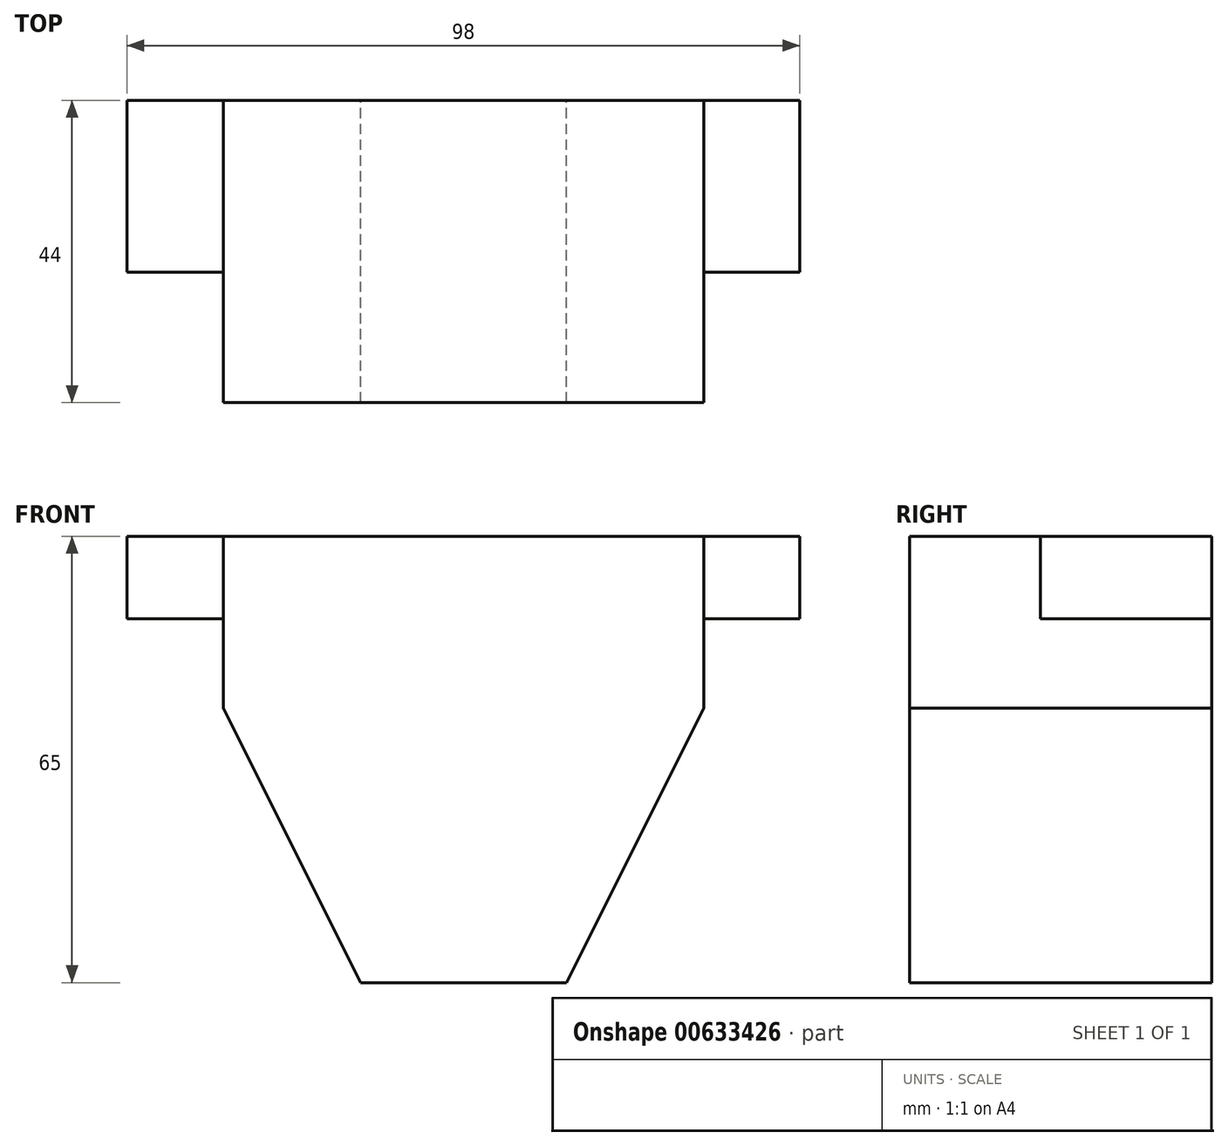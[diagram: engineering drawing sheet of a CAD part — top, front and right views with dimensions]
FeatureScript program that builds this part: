
annotation { "Feature Type Name" : "Feature", "Feature Type Description" : "" }
export const myFeature = defineFeature(function(context is Context, id is Id, definition is map)
    precondition{}
    {
        {
            var Q0;
            Q0=qCreatedBy(makeId("Front.planeOp"),FACE);
            var sketch = newSketch(context, id + "F0", { "sketchPlane" : qUnion([Q0])});
            skLineSegment(sketch, "E0.bottom", {"start": v(-35, -12.5) * mm, "end": v(35, -12.5) * mm});
            skLineSegment(sketch, "E0.top", {"start": v(-35, 12.5) * mm, "end": v(35, 12.5) * mm});
            skLineSegment(sketch, "E0.left", {"start": v(-35, -12.5) * mm, "end": v(-35, 12.5) * mm});
            skLineSegment(sketch, "E0.right", {"start": v(35, -12.5) * mm, "end": v(35, 12.5) * mm});
            skPoint(sketch, "E0.middle", {"position": v(0, 0) * mm});
            skLineSegment(sketch, "E1", {"start": v(-35, 12.5) * mm, "end": v(-49, 12.5) * mm});
            skLineSegment(sketch, "E2", {"start": v(-49, 12.5) * mm, "end": v(-49, 0.5) * mm});
            skLineSegment(sketch, "E3", {"start": v(-49, 0.5) * mm, "end": v(-35, 0.5) * mm});
            skLineSegment(sketch, "E4", {"start": v(35, 12.5) * mm, "end": v(49, 12.5) * mm});
            skLineSegment(sketch, "E5", {"start": v(49, 12.5) * mm, "end": v(49, 0.5) * mm});
            skLineSegment(sketch, "E6", {"start": v(49, 0.5) * mm, "end": v(35, 0.5) * mm});
            skLineSegment(sketch, "E7", {"start": v(-15, -52.5) * mm, "end": v(15, -52.5) * mm});
            skLineSegment(sketch, "E8", {"start": v(-15, -52.5) * mm, "end": v(-35, -12.5) * mm});
            skLineSegment(sketch, "E9", {"start": v(35, -12.5) * mm, "end": v(15, -52.5) * mm});
            skSolve(sketch);
        }
        {
            var Q0;
            {var subQ0=sQuery(id+"F0.wireOp",EDGE,"E1");Q0=makeQuery(id+"F0.imprint","IMPRINT",FACE,{"disambiguationData":[TD([[makeQuery(id+"F0.imprint","IMPRINT",EDGE,{"derivedFrom":subQ0}),1.0]])]});}
            var Q1;
            {var subQ0=sQuery(id+"F0.wireOp",EDGE,"E4");Q1=makeQuery(id+"F0.imprint","IMPRINT",FACE,{"disambiguationData":[TD([[makeQuery(id+"F0.imprint","IMPRINT",EDGE,{"derivedFrom":subQ0}),-1.0]])]});}
            extrude(context, id + "F1", {"entities" : qUnion([Q0, Q1]), "depth" : 25 * mm, "offsetDistance" : 25 * mm});
        }
        {
            var Q0;
            {var subQ3=sQuery(id+"F0.wireOp",EDGE,"E0.bottom");Q0=makeQuery(id+"F0.imprint","IMPRINT",FACE,{"disambiguationData":[TD([[makeQuery(id+"F0.imprint","IMPRINT",EDGE,{"derivedFrom":subQ3}),1.0]])]});}
            var Q1;
            Q1=makeQuery(id+"F0.imprint","IMPRINT",FACE,{"disambiguationData":[TD([[makeQuery(id+"F0.imprint","IMPRINT",EDGE,{"derivedFrom":sQuery(id+"F0.wireOp",EDGE,"E0.bottom")}),-1.0]])]});
            extrude(context, id + "F2", {"entities" : qUnion([Q0, Q1]), "depth" : 44 * mm, "offsetDistance" : 25 * mm});
        }
    });
